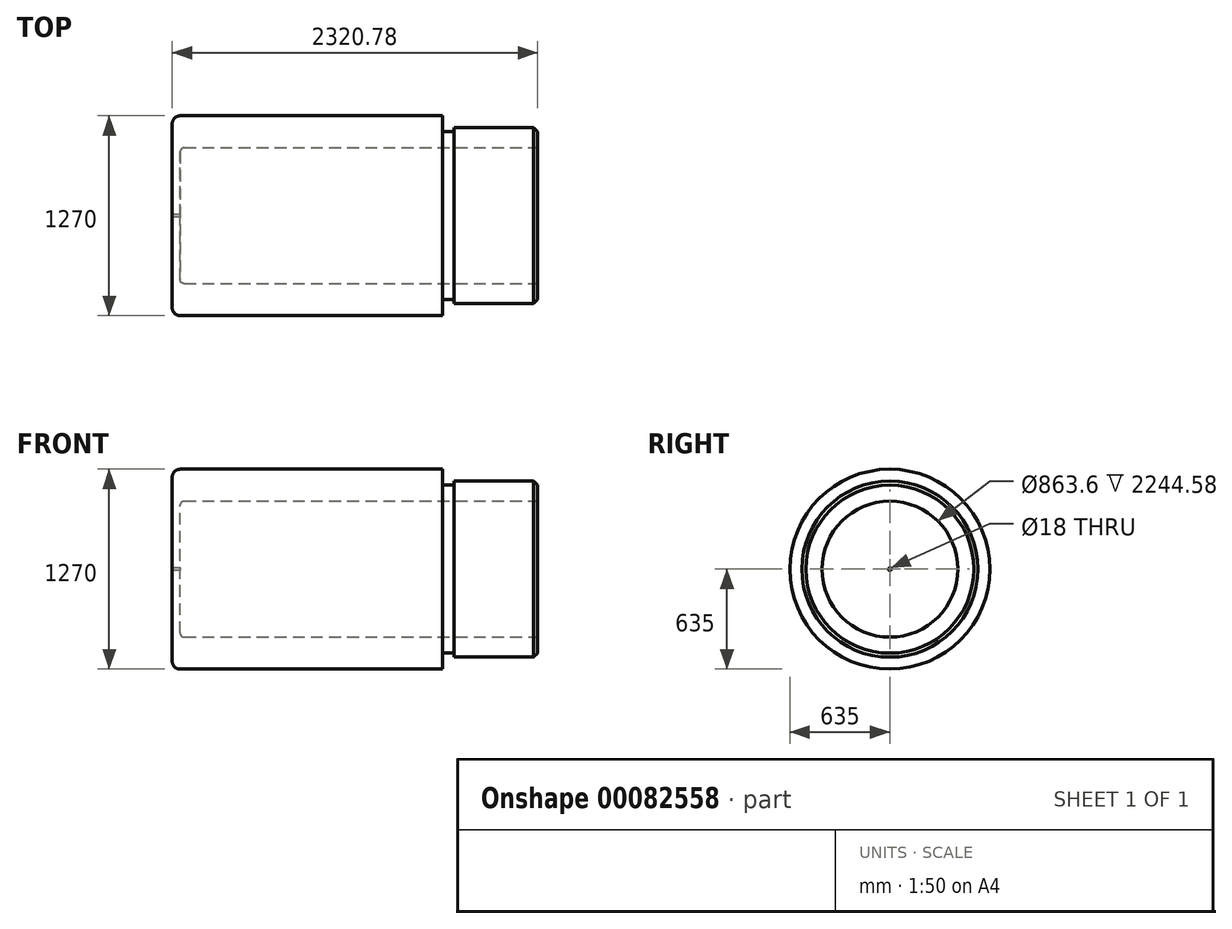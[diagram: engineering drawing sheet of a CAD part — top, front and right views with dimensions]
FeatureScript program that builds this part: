
annotation { "Feature Type Name" : "Feature", "Feature Type Description" : "" }
export const myFeature = defineFeature(function(context is Context, id is Id, definition is map)
    precondition{}
    {
        {
            var Q0;
            Q0=qCreatedBy(makeId("Front.planeOp"),FACE);
            var sketch = newSketch(context, id + "F0", { "sketchPlane" : qUnion([Q0])});
            skLineSegment(sketch, "E0", {"start": v(0, 0) * mm, "end": v(0, 584.2) * mm});
            skLineSegment(sketch, "E1", {"start": v(50.8, 635) * mm, "end": v(1716.22, 635) * mm});
            skLineSegment(sketch, "E2", {"start": v(1716.22, 635) * mm, "end": v(1716.22, 533.4) * mm});
            skLineSegment(sketch, "E3", {"start": v(1790.07, 533.4) * mm, "end": v(1790.07, 558.8) * mm});
            skLineSegment(sketch, "E4", {"start": v(1790.07, 558.8) * mm, "end": v(2295.38, 558.8) * mm});
            skLineSegment(sketch, "E5", {"start": v(2295.38, 558.8) * mm, "end": v(2320.78, 533.4) * mm});
            skLineSegment(sketch, "E6", {"start": v(2320.78, 533.4) * mm, "end": v(2320.78, 431.8) * mm});
            skLineSegment(sketch, "E7", {"start": v(2320.78, 431.8) * mm, "end": v(1618.65, 431.8) * mm});
            skLineSegment(sketch, "E8", {"start": v(1618.65, 431.8) * mm, "end": v(76.2, 431.8) * mm});
            skLineSegment(sketch, "E9", {"start": v(50.8, 406.4) * mm, "end": v(50.8, 0) * mm});
            skLineSegment(sketch, "E10", {"start": v(50.8, 0) * mm, "end": v(0, 0) * mm});
            skLineSegment(sketch, "E11", {"start": v(1790.07, 533.4) * mm, "end": v(1716.22, 533.4) * mm});
            skPoint(sketch, "E12.visualSharp", {"position": v(50.8, 431.8) * mm});
            skArc(sketch, "E12.filletArc", {"start": v(76.2, 431.8) * mm, "mid": v(58.24, 424.36) * mm, "end": v(50.8, 406.4) * mm});
            skPoint(sketch, "E13.visualSharp", {"position": v(0, 635) * mm});
            skArc(sketch, "E13.filletArc", {"start": v(50.8, 635) * mm, "mid": v(14.88, 620.12) * mm, "end": v(0, 584.2) * mm});
            skSolve(sketch);
        }
        {
            var Q0;
            Q0=makeQuery(id+"F0.imprint","IMPRINT",FACE,{"disambiguationData":[TD([[makeQuery(id+"F0.imprint","IMPRINT",EDGE,{"derivedFrom":sQuery(id+"F0.wireOp",EDGE,"E0")}),-1.0]])]});
            var Q1;
            Q1=sQuery(id+"F0.wireOp",EDGE,"E10");
            revolve(context, id + "F1", {"entities" : qUnion([Q0]), "axis" : qUnion([Q1]), "revolveType" : RevolveType.FULL});
        }
        {
            var Q0;
            Q0=makeQuery(id+"F1.opRevolve","SWEPT_FACE",FACE,{"disambiguationData":[OSD([sQuery(id+"F0.wireOp",EDGE,"E0")])]});
            var sketch = newSketch(context, id + "F2", { "sketchPlane" : qUnion([Q0])});
            skPoint(sketch, "E14", {"position": v(0, 0) * mm});
            skSolve(sketch);
        }
        {
            var Q0;
            Q0=sQuery(id+"F2.wireOp",VERTEX,"E14");
            var Q1;
            Q1=makeQuery(id+"F1.opRevolve","SWEPT_BODY",BODY,{"disambiguationData":[OSD([sQuery(id+"F0.wireOp",EDGE,"E0"),sQuery(id+"F0.wireOp",EDGE,"E1"),sQuery(id+"F0.wireOp",EDGE,"E2"),sQuery(id+"F0.wireOp",EDGE,"E3"),sQuery(id+"F0.wireOp",EDGE,"E4"),sQuery(id+"F0.wireOp",EDGE,"E5"),sQuery(id+"F0.wireOp",EDGE,"E6"),sQuery(id+"F0.wireOp",EDGE,"E7"),sQuery(id+"F0.wireOp",EDGE,"E8"),sQuery(id+"F0.wireOp",EDGE,"E9"),sQuery(id+"F0.wireOp",EDGE,"E10"),sQuery(id+"F0.wireOp",EDGE,"E11"),sQuery(id+"F0.wireOp",EDGE,"E12.filletArc"),sQuery(id+"F0.wireOp",EDGE,"E13.filletArc")])]});
            hole(context, id + "F3", {"style" : HoleStyle.SIMPLE, "endStyle" : HoleEndStyle.THROUGH, "standardTappedOrClearance" : lookupTablePath({ "standard" : "ISO", "engagement" : "75%", "pitch" : "2 mm", "size" : "M20", "type" : "Tapped" }), "standardBlindInLast" : lookupTablePath({ "standard" : "ISO", "engagement" : "75%", "pitch" : "2 mm", "size" : "M20", "type" : "Tapped" }), "holeDiameter" : 18 * mm, "locations" : qUnion([Q0]), "scope" : qUnion([Q1]), "isTappedThrough" : true, "majorDiameter" : 20 * mm, "showTappedDepth" : true});
        }
    });
